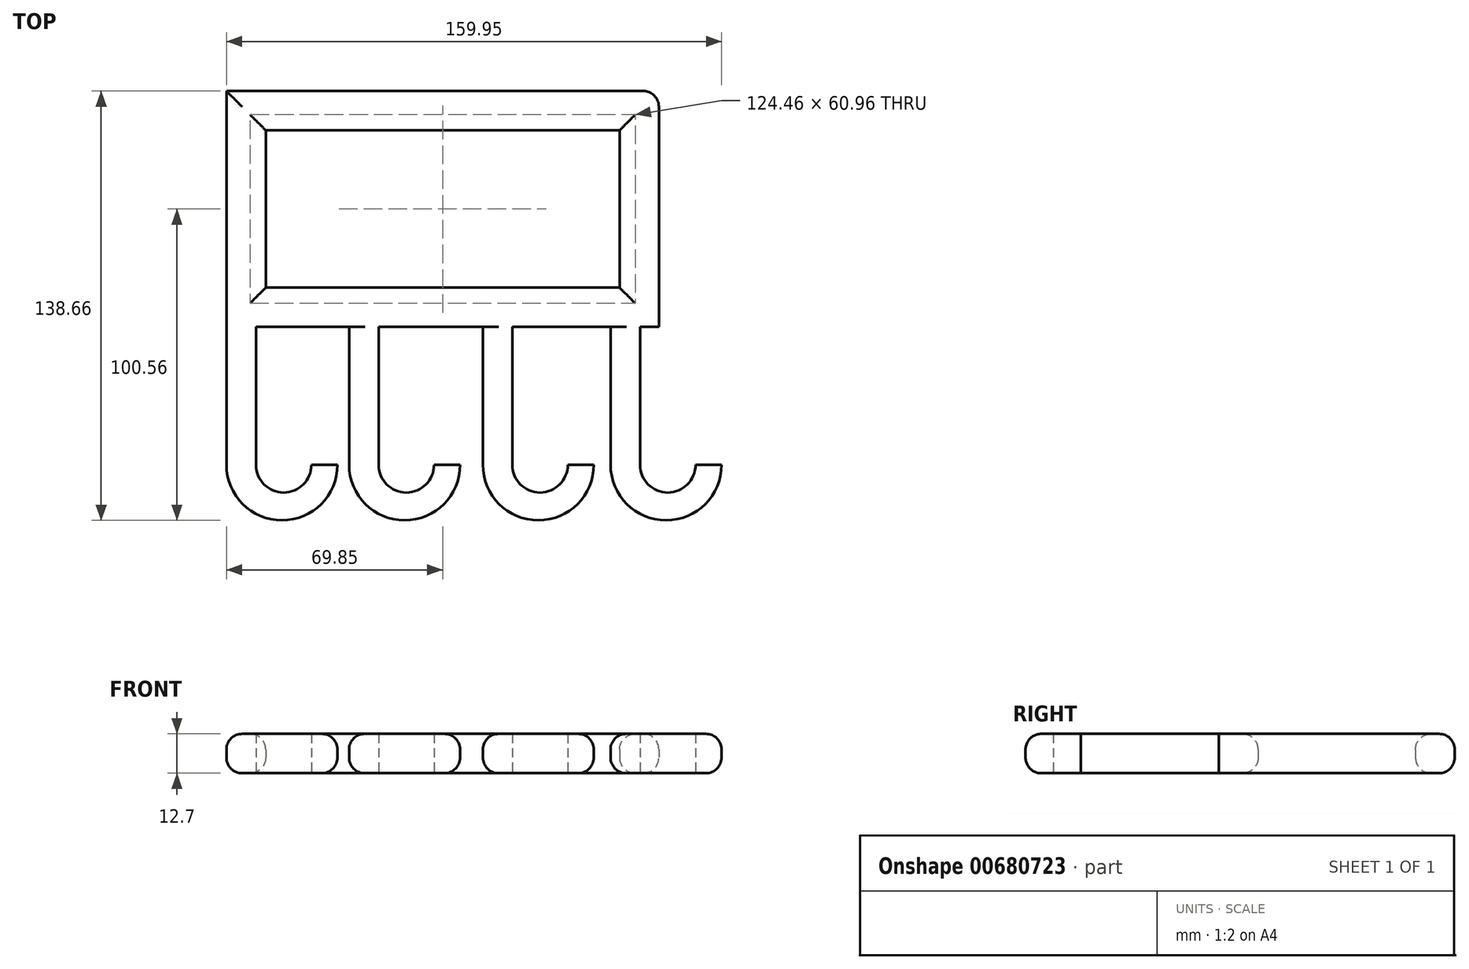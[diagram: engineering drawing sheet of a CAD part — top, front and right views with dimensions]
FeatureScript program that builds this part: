
annotation { "Feature Type Name" : "Feature", "Feature Type Description" : "" }
export const myFeature = defineFeature(function(context is Context, id is Id, definition is map)
    precondition{}
    {
        {
            var Q0;
            Q0=qCreatedBy(makeId("Top.planeOp"),FACE);
            var sketch = newSketch(context, id + "F0", { "sketchPlane" : qUnion([Q0])});
            skLineSegment(sketch, "E0.bottom", {"start": v(69.85, 38.1) * mm, "end": v(-69.85, 38.1) * mm});
            skLineSegment(sketch, "E0.top", {"start": v(69.85, -38.1) * mm, "end": v(-69.85, -38.1) * mm});
            skLineSegment(sketch, "E0.left", {"start": v(69.85, 38.1) * mm, "end": v(69.85, -38.1) * mm});
            skLineSegment(sketch, "E0.right", {"start": v(-69.85, 38.1) * mm, "end": v(-69.85, -38.1) * mm});
            skPoint(sketch, "E0.middle", {"position": v(0, 0) * mm});
            skLineSegment(sketch, "E1.bottom", {"start": v(57.15, 25.4) * mm, "end": v(-57.15, 25.4) * mm});
            skLineSegment(sketch, "E1.top", {"start": v(57.15, -25.4) * mm, "end": v(-57.15, -25.4) * mm});
            skLineSegment(sketch, "E1.left", {"start": v(57.15, 25.4) * mm, "end": v(57.15, -25.4) * mm});
            skLineSegment(sketch, "E1.right", {"start": v(-57.15, 25.4) * mm, "end": v(-57.15, -25.4) * mm});
            skLineSegment(sketch, "E2", {"start": v(-69.85, -38.1) * mm, "end": v(-69.85, -82.63) * mm});
            skArc(sketch, "E3", {"start": v(-69.85, -82.63) * mm, "mid": v(-51.92, -100.56) * mm, "end": v(-33.99, -82.63) * mm});
            skPoint(sketch, "E4", {"position": v(-33.99, -82.63) * mm});
            skPoint(sketch, "E5", {"position": v(-69.85, -82.63) * mm});
            skPoint(sketch, "E6", {"position": v(-60.33, -82.63) * mm});
            skPoint(sketch, "E7", {"position": v(-42.4, -82.63) * mm});
            skArc(sketch, "E8", {"start": v(-60.33, -82.63) * mm, "mid": v(-51.36, -91.6) * mm, "end": v(-42.4, -82.63) * mm});
            skLineSegment(sketch, "E9", {"start": v(-60.33, -82.63) * mm, "end": v(-60.33, -38.1) * mm});
            skLineSegment(sketch, "E10", {"start": v(-42.4, -82.63) * mm, "end": v(-33.99, -82.63) * mm});
            skLineSegment(sketch, "E11", {"start": v(-34.93, -38.1) * mm, "end": v(0, -38.1) * mm});
            skLineSegment(sketch, "E12", {"start": v(-69.85, 38.1) * mm, "end": v(-69.85, -38.1) * mm, "construction": true});
            skLineSegment(sketch, "E13", {"start": v(-69.85, 0) * mm, "end": v(69.85, 0) * mm, "construction": true});
            skLineSegment(sketch, "E14", {"start": v(0, 0) * mm, "end": v(69.85, 0) * mm, "construction": true});
            skLineSegment(sketch, "E15", {"start": v(34.93, 0) * mm, "end": v(34.93, -38.1) * mm, "construction": true});
            skLineSegment(sketch, "E16", {"start": v(0, 0) * mm, "end": v(0, -38.1) * mm, "construction": true});
            skLineSegment(sketch, "E17", {"start": v(0, -38.1) * mm, "end": v(0, 0) * mm, "construction": true});
            skLineSegment(sketch, "E18", {"start": v(-69.85, 0) * mm, "end": v(0, 0) * mm, "construction": true});
            skLineSegment(sketch, "E19", {"start": v(-34.93, 0) * mm, "end": v(-34.93, -38.1) * mm, "construction": true});
            skLineSegment(sketch, "E20", {"start": v(-30.23, -38.1) * mm, "end": v(-30.23, -82.63) * mm});
            skArc(sketch, "E21", {"start": v(-30.23, -82.63) * mm, "mid": v(-12.3, -100.56) * mm, "end": v(5.63, -82.63) * mm});
            skPoint(sketch, "E22", {"position": v(5.63, -82.63) * mm});
            skPoint(sketch, "E23", {"position": v(-30.23, -82.63) * mm});
            skPoint(sketch, "E24", {"position": v(-20.7, -82.63) * mm});
            skPoint(sketch, "E25", {"position": v(-2.78, -82.63) * mm});
            skArc(sketch, "E26", {"start": v(-20.7, -82.63) * mm, "mid": v(-11.74, -91.6) * mm, "end": v(-2.78, -82.63) * mm});
            skLineSegment(sketch, "E27", {"start": v(-20.7, -82.63) * mm, "end": v(-20.7, -38.1) * mm});
            skLineSegment(sketch, "E28", {"start": v(-2.78, -82.63) * mm, "end": v(5.63, -82.63) * mm});
            skLineSegment(sketch, "E29", {"start": v(12.98, -38.1) * mm, "end": v(12.98, -82.63) * mm});
            skArc(sketch, "E30", {"start": v(12.98, -82.63) * mm, "mid": v(30.91, -100.56) * mm, "end": v(48.84, -82.63) * mm});
            skPoint(sketch, "E31", {"position": v(48.84, -82.63) * mm});
            skPoint(sketch, "E32", {"position": v(12.98, -82.63) * mm});
            skPoint(sketch, "E33", {"position": v(22.5, -82.63) * mm});
            skPoint(sketch, "E34", {"position": v(40.44, -82.63) * mm});
            skArc(sketch, "E35", {"start": v(22.5, -82.63) * mm, "mid": v(31.47, -91.6) * mm, "end": v(40.44, -82.63) * mm});
            skLineSegment(sketch, "E36", {"start": v(22.5, -82.63) * mm, "end": v(22.5, -38.1) * mm});
            skLineSegment(sketch, "E37", {"start": v(40.44, -82.63) * mm, "end": v(48.84, -82.63) * mm});
            skLineSegment(sketch, "E38", {"start": v(54.24, -38.1) * mm, "end": v(54.24, -82.63) * mm});
            skArc(sketch, "E39", {"start": v(54.24, -82.63) * mm, "mid": v(72.17, -100.56) * mm, "end": v(90.1, -82.63) * mm});
            skPoint(sketch, "E40", {"position": v(90.1, -82.63) * mm});
            skPoint(sketch, "E41", {"position": v(54.24, -82.63) * mm});
            skPoint(sketch, "E42", {"position": v(63.77, -82.63) * mm});
            skPoint(sketch, "E43", {"position": v(81.7, -82.63) * mm});
            skArc(sketch, "E44", {"start": v(63.77, -82.63) * mm, "mid": v(72.73, -91.6) * mm, "end": v(81.7, -82.63) * mm});
            skLineSegment(sketch, "E45", {"start": v(63.77, -82.63) * mm, "end": v(63.77, -38.1) * mm});
            skLineSegment(sketch, "E46", {"start": v(81.7, -82.63) * mm, "end": v(90.1, -82.63) * mm});
            skLineSegment(sketch, "E47", {"start": v(-30.23, -38.1) * mm, "end": v(-20.7, -38.1) * mm});
            skLineSegment(sketch, "E48", {"start": v(12.98, -38.1) * mm, "end": v(22.5, -38.1) * mm});
            skLineSegment(sketch, "E49", {"start": v(54.24, -38.1) * mm, "end": v(63.77, -38.1) * mm});
            skLineSegment(sketch, "E50", {"start": v(-60.33, -38.1) * mm, "end": v(69.85, -38.1) * mm, "construction": true});
            skLineSegment(sketch, "E51", {"start": v(69.85, -38.1) * mm, "end": v(79.38, -38.1) * mm, "construction": true});
            skLineSegment(sketch, "E52", {"start": v(79.38, -38.1) * mm, "end": v(-60.33, -38.1) * mm, "construction": true});
            skLineSegment(sketch, "E53", {"start": v(9.53, -38.1) * mm, "end": v(-60.33, -38.1) * mm, "construction": true});
            skSolve(sketch);
        }
        {
            var Q0;
            Q0 = qSketchRegion(id + "F0", true);
            extrude(context, id + "F1", {"entities" : qUnion([Q0]), "depth" : 12.7 * mm, "offsetDistance" : 25.4 * mm});
        }
        {
            var Q0;
            Q0=makeQuery(id+"F1.opExtrude","CAP_EDGE",EDGE,{"disambiguationData":[OSD([sQuery(id+"F0.wireOp",EDGE,"E1.bottom")])],"isStart":false});
            var Q1;
            Q1=makeQuery(id+"F1.opExtrude","CAP_EDGE",EDGE,{"disambiguationData":[OSD([sQuery(id+"F0.wireOp",EDGE,"E1.right")])],"isStart":false});
            var Q2;
            Q2=makeQuery(id+"F1.opExtrude","CAP_EDGE",EDGE,{"disambiguationData":[OSD([sQuery(id+"F0.wireOp",EDGE,"E1.top")])],"isStart":false});
            var Q3;
            Q3=makeQuery(id+"F1.opExtrude","CAP_EDGE",EDGE,{"disambiguationData":[OSD([sQuery(id+"F0.wireOp",EDGE,"E1.left")])],"isStart":false});
            var Q4;
            Q4=makeQuery(id+"F1.opExtrude","CAP_EDGE",EDGE,{"disambiguationData":[OSD([sQuery(id+"F0.wireOp",EDGE,"E0.bottom")])],"isStart":false});
            var Q5;
            Q5=makeQuery(id+"F1.opExtrude","SWEPT_EDGE",EDGE,{"disambiguationData":[OSD([sQuery(id+"F0.wireOp",EDGE,"E0.bottom"),sQuery(id+"F0.wireOp",EDGE,"E0.left")])]});
            var Q6;
            Q6=makeQuery(id+"F1.opExtrude","CAP_EDGE",EDGE,{"disambiguationData":[OSD([sQuery(id+"F0.wireOp",EDGE,"E0.left")])],"isStart":false});
            var Q7;
            Q7=makeQuery(id+"F1.opExtrude","CAP_EDGE",EDGE,{"disambiguationData":[OSD([sQuery(id+"F0.wireOp",EDGE,"E0.left")])],"isStart":true});
            var Q8;
            Q8=makeQuery(id+"F1.opExtrude","CAP_EDGE",EDGE,{"disambiguationData":[OSD([sQuery(id+"F0.wireOp",EDGE,"E0.bottom")])],"isStart":true});
            var Q9;
            Q9=makeQuery(id+"F1.opExtrude","CAP_EDGE",EDGE,{"disambiguationData":[OSD([sQuery(id+"F0.wireOp",EDGE,"E1.top")])],"isStart":true});
            var Q10;
            Q10=makeQuery(id+"F1.opExtrude","CAP_EDGE",EDGE,{"disambiguationData":[OSD([sQuery(id+"F0.wireOp",EDGE,"E1.left")])],"isStart":true});
            var Q11;
            Q11=makeQuery(id+"F1.opExtrude","CAP_EDGE",EDGE,{"disambiguationData":[OSD([sQuery(id+"F0.wireOp",EDGE,"E1.bottom")])],"isStart":true});
            var Q12;
            Q12=makeQuery(id+"F1.opExtrude","CAP_EDGE",EDGE,{"disambiguationData":[OSD([sQuery(id+"F0.wireOp",EDGE,"E1.right")])],"isStart":true});
            var Q13;
            Q13=makeQuery(id+"F1.opExtrude","CAP_EDGE",EDGE,{"disambiguationData":[OSD([sQuery(id+"F0.wireOp",EDGE,"E0.right"),sQuery(id+"F0.wireOp",EDGE,"E2")])],"isStart":true});
            var Q14;
            Q14=makeQuery(id+"F1.opExtrude","CAP_EDGE",EDGE,{"disambiguationData":[OSD([sQuery(id+"F0.wireOp",EDGE,"E0.right"),sQuery(id+"F0.wireOp",EDGE,"E2")])],"isStart":false});
            var Q15;
            Q15=makeQuery(id+"F1.opExtrude","CAP_EDGE",EDGE,{"disambiguationData":[OSD([sQuery(id+"F0.wireOp",EDGE,"E20")])],"isStart":false});
            var Q16;
            Q16=makeQuery(id+"F1.opExtrude","CAP_EDGE",EDGE,{"disambiguationData":[OSD([sQuery(id+"F0.wireOp",EDGE,"E20")])],"isStart":true});
            var Q17;
            Q17=makeQuery(id+"F1.opExtrude","CAP_EDGE",EDGE,{"disambiguationData":[OSD([sQuery(id+"F0.wireOp",EDGE,"E29")])],"isStart":false});
            var Q18;
            Q18=makeQuery(id+"F1.opExtrude","CAP_EDGE",EDGE,{"disambiguationData":[OSD([sQuery(id+"F0.wireOp",EDGE,"E29")])],"isStart":true});
            var Q19;
            Q19=makeQuery(id+"F1.opExtrude","CAP_EDGE",EDGE,{"disambiguationData":[OSD([sQuery(id+"F0.wireOp",EDGE,"E38")])],"isStart":false});
            var Q20;
            Q20=makeQuery(id+"F1.opExtrude","CAP_EDGE",EDGE,{"disambiguationData":[OSD([sQuery(id+"F0.wireOp",EDGE,"E38")])],"isStart":true});
            fillet(context, id + "F2", {"entities" : qUnion([Q0, Q1, Q2, Q3, Q4, Q5, Q6, Q7, Q8, Q9, Q10, Q11, Q12, Q13, Q14, Q15, Q16, Q17, Q18, Q19, Q20]), "radius" : 5.08 * mm, "tangentPropagation" : true, "allowEdgeOverflow" : false});
        }
    });
